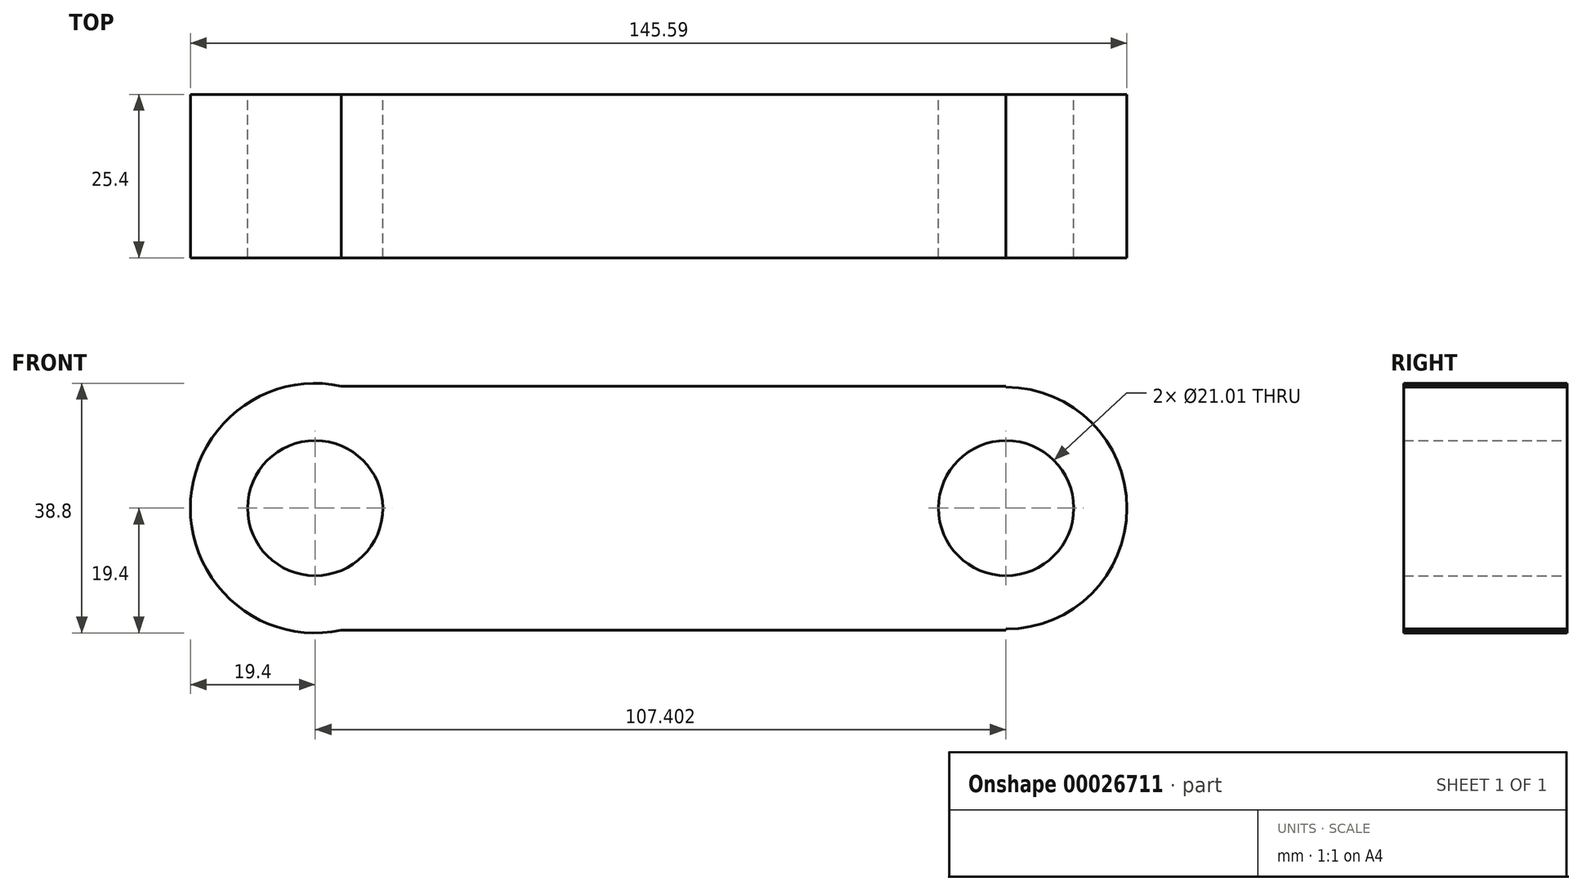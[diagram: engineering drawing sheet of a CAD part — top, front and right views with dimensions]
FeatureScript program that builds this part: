
annotation { "Feature Type Name" : "Feature", "Feature Type Description" : "" }
export const myFeature = defineFeature(function(context is Context, id is Id, definition is map)
    precondition{}
    {
        {
            var Q0;
            Q0=qCreatedBy(makeId("Front.planeOp"),FACE);
            var sketch = newSketch(context, id + "F0", { "sketchPlane" : qUnion([Q0])});
            skLineSegment(sketch, "E0.bottom", {"start": v(-42.64, 34.53) * mm, "end": v(64.76, 34.53) * mm});
            skLineSegment(sketch, "E0.top", {"start": v(-42.64, -3.43) * mm, "end": v(64.76, -3.43) * mm});
            skLineSegment(sketch, "E0.right", {"start": v(64.76, 34.53) * mm, "end": v(64.76, 34.34) * mm});
            skArc(sketch, "E1", {"start": v(64.76, -3.24) * mm, "mid": v(83.55, 15.55) * mm, "end": v(64.76, 34.34) * mm});
            skArc(sketch, "E2", {"start": v(-38.6, 34.53) * mm, "mid": v(-62.04, 15.55) * mm, "end": v(-38.6, -3.43) * mm});
            skLineSegment(sketch, "E3.trimOffspring", {"start": v(64.76, -3.24) * mm, "end": v(64.76, -3.43) * mm});
            skCircle(sketch, "E4", {"center": v(64.76, 15.55) * mm, "radius": 10.5 * mm});
            skCircle(sketch, "E5", {"center": v(-42.64, 15.55) * mm, "radius": 10.5 * mm});
            skSolve(sketch);
        }
        {
            var Q0;
            {var subQ2=sQuery(id+"F0.wireOp",EDGE,"E0.right");Q0=makeQuery(id+"F0.imprint","IMPRINT",FACE,{"disambiguationData":[TD([[makeQuery(id+"F0.imprint","IMPRINT",EDGE,{"derivedFrom":subQ2}),-1.0]])]});}
            extrude(context, id + "F1", {"entities" : qUnion([Q0]), "depth" : 25.4 * mm});
        }
    });
